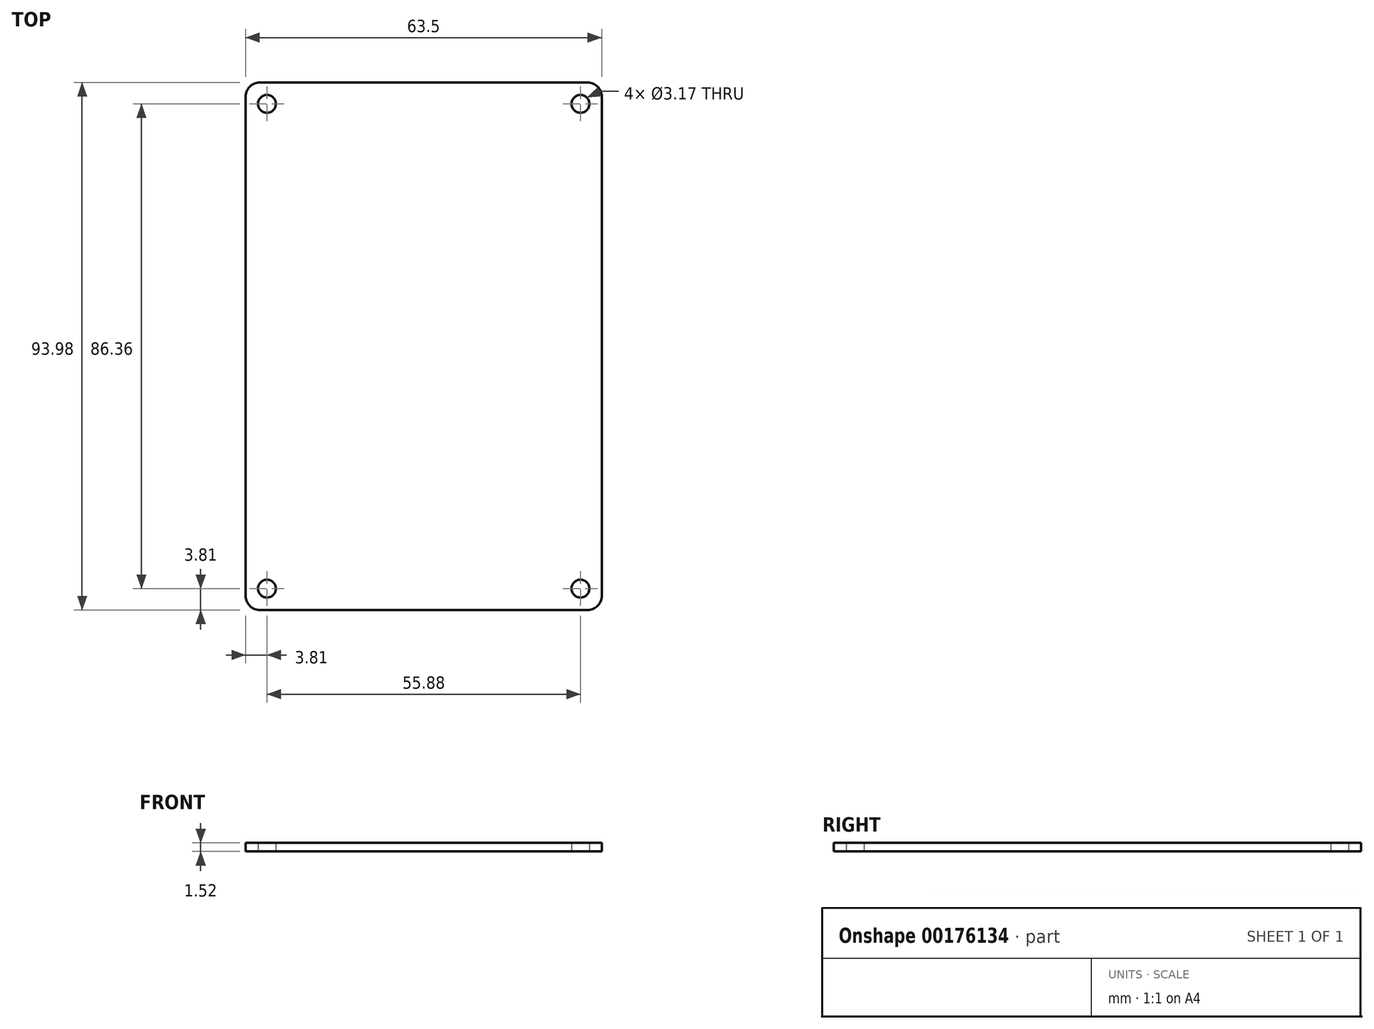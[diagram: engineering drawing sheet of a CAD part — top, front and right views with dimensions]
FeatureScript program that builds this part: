
annotation { "Feature Type Name" : "Feature", "Feature Type Description" : "" }
export const myFeature = defineFeature(function(context is Context, id is Id, definition is map)
    precondition{}
    {
        {
            var Q0;
            Q0=qCreatedBy(makeId("Top.planeOp"),FACE);
            var sketch = newSketch(context, id + "F0", { "sketchPlane" : qUnion([Q0])});
            skLineSegment(sketch, "E0.bottom", {"start": v(-31.75, 46.99) * mm, "end": v(31.75, 46.99) * mm});
            skLineSegment(sketch, "E0.top", {"start": v(-31.75, -47) * mm, "end": v(31.75, -47) * mm});
            skLineSegment(sketch, "E0.left", {"start": v(-31.75, 46.99) * mm, "end": v(-31.75, -47) * mm});
            skLineSegment(sketch, "E0.right", {"start": v(31.75, 46.99) * mm, "end": v(31.75, -47) * mm});
            skPoint(sketch, "E0.middle", {"position": v(0, 0) * mm});
            skLineSegment(sketch, "E1.bottom", {"start": v(-27.94, 43.18) * mm, "end": v(27.94, 43.18) * mm, "construction": true});
            skLineSegment(sketch, "E1.top", {"start": v(-27.94, -43.18) * mm, "end": v(27.94, -43.18) * mm, "construction": true});
            skLineSegment(sketch, "E1.left", {"start": v(-27.94, 43.18) * mm, "end": v(-27.94, -43.18) * mm, "construction": true});
            skLineSegment(sketch, "E1.right", {"start": v(27.94, 43.18) * mm, "end": v(27.94, -43.18) * mm, "construction": true});
            skCircle(sketch, "E2", {"center": v(-27.94, 43.18) * mm, "radius": 1.59 * mm});
            skCircle(sketch, "E3", {"center": v(27.94, 43.18) * mm, "radius": 1.59 * mm});
            skCircle(sketch, "E4", {"center": v(27.94, -43.18) * mm, "radius": 1.59 * mm});
            skCircle(sketch, "E5", {"center": v(-27.94, -43.18) * mm, "radius": 1.59 * mm});
            skSolve(sketch);
        }
        {
            var Q0;
            Q0 = qSketchRegion(id + "F0", true);
            extrude(context, id + "F1", {"entities" : qUnion([Q0]), "depth" : 1.52 * mm});
        }
        {
            var Q0;
            Q0=makeQuery(id+"F1.opExtrude","SWEPT_EDGE",EDGE,{"disambiguationData":[OSD([sQuery(id+"F0.wireOp",EDGE,"E0.top"),sQuery(id+"F0.wireOp",EDGE,"E0.left")])]});
            var Q1;
            Q1=makeQuery(id+"F1.opExtrude","SWEPT_EDGE",EDGE,{"disambiguationData":[OSD([sQuery(id+"F0.wireOp",EDGE,"E0.top"),sQuery(id+"F0.wireOp",EDGE,"E0.right")])]});
            var Q2;
            Q2=makeQuery(id+"F1.opExtrude","SWEPT_EDGE",EDGE,{"disambiguationData":[OSD([sQuery(id+"F0.wireOp",EDGE,"E0.bottom"),sQuery(id+"F0.wireOp",EDGE,"E0.left")])]});
            var Q3;
            Q3=makeQuery(id+"F1.opExtrude","SWEPT_EDGE",EDGE,{"disambiguationData":[OSD([sQuery(id+"F0.wireOp",EDGE,"E0.bottom"),sQuery(id+"F0.wireOp",EDGE,"E0.right")])]});
            fillet(context, id + "F2", {"entities" : qUnion([Q0, Q1, Q2, Q3]), "radius" : 2.54 * mm, "tangentPropagation" : true, "allowEdgeOverflow" : false});
        }
    });
